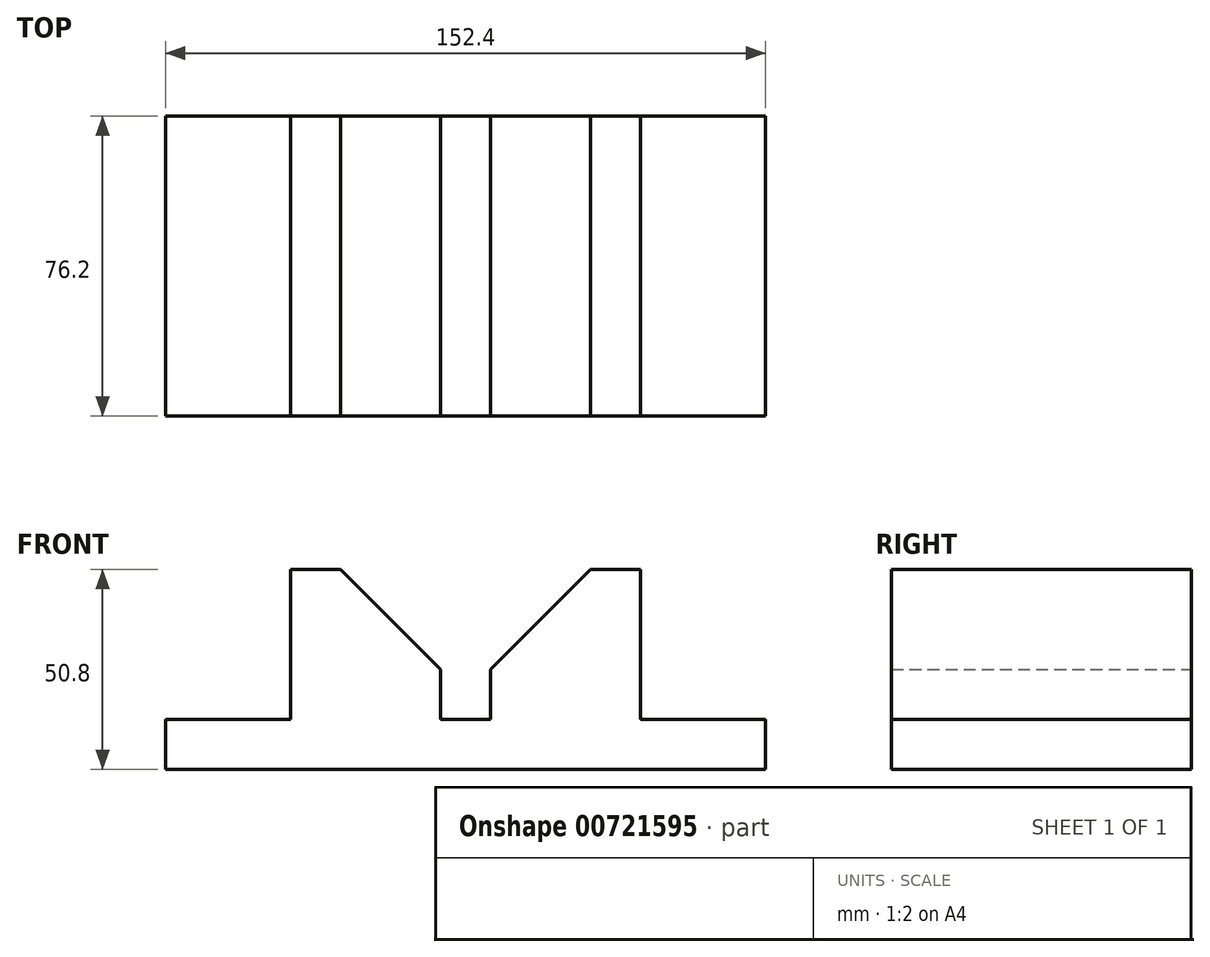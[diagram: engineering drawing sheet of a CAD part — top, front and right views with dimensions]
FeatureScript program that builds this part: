
annotation { "Feature Type Name" : "Feature", "Feature Type Description" : "" }
export const myFeature = defineFeature(function(context is Context, id is Id, definition is map)
    precondition{}
    {
        {
            var Q0;
            Q0=qCreatedBy(makeId("Front.planeOp"),FACE);
            var sketch = newSketch(context, id + "F0", { "sketchPlane" : qUnion([Q0])});
            skLineSegment(sketch, "E0.bottom", {"start": v(-81.5, 18.15) * mm, "end": v(-49.76, 18.15) * mm});
            skLineSegment(sketch, "E0.top", {"start": v(-81.5, 5.45) * mm, "end": v(70.9, 5.45) * mm});
            skLineSegment(sketch, "E0.left", {"start": v(-81.5, 18.15) * mm, "end": v(-81.5, 5.45) * mm});
            skLineSegment(sketch, "E0.right", {"start": v(70.9, 18.15) * mm, "end": v(70.9, 5.45) * mm});
            skLineSegment(sketch, "E1", {"start": v(70.9, 18.15) * mm, "end": v(39.14, 18.15) * mm});
            skLineSegment(sketch, "E2", {"start": v(-49.76, 18.15) * mm, "end": v(-81.5, 18.15) * mm});
            skLineSegment(sketch, "E3", {"start": v(-49.76, 18.15) * mm, "end": v(-49.76, 56.25) * mm});
            skLineSegment(sketch, "E4", {"start": v(39.14, 18.15) * mm, "end": v(39.14, 56.25) * mm});
            skLineSegment(sketch, "E5", {"start": v(-49.76, 56.25) * mm, "end": v(-37.06, 56.25) * mm});
            skLineSegment(sketch, "E6", {"start": v(26.44, 56.25) * mm, "end": v(39.14, 56.25) * mm});
            skLineSegment(sketch, "E7", {"start": v(-11.66, 30.85) * mm, "end": v(-11.66, 18.15) * mm});
            skLineSegment(sketch, "E8", {"start": v(1.04, 30.85) * mm, "end": v(1.04, 18.15) * mm});
            skLineSegment(sketch, "E9", {"start": v(-37.06, 56.25) * mm, "end": v(-11.66, 30.85) * mm});
            skLineSegment(sketch, "E10", {"start": v(1.04, 30.85) * mm, "end": v(26.44, 56.25) * mm});
            skLineSegment(sketch, "E11.trimOffspring", {"start": v(-11.66, 18.15) * mm, "end": v(1.04, 18.15) * mm});
            skLineSegment(sketch, "E12.trimOffspring", {"start": v(39.14, 18.15) * mm, "end": v(70.9, 18.15) * mm});
            skSolve(sketch);
        }
        {
            var Q0;
            Q0=makeQuery(id+"F0.imprint","IMPRINT",FACE,{"disambiguationData":[TD([[makeQuery(id+"F0.imprint","IMPRINT",EDGE,{"derivedFrom":sQuery(id+"F0.wireOp",EDGE,"E0.top")}),1.0]])]});
            extrude(context, id + "F1", {"entities" : qUnion([Q0]), "depth" : 76.2 * mm, "offsetDistance" : 25.4 * mm});
        }
    });
